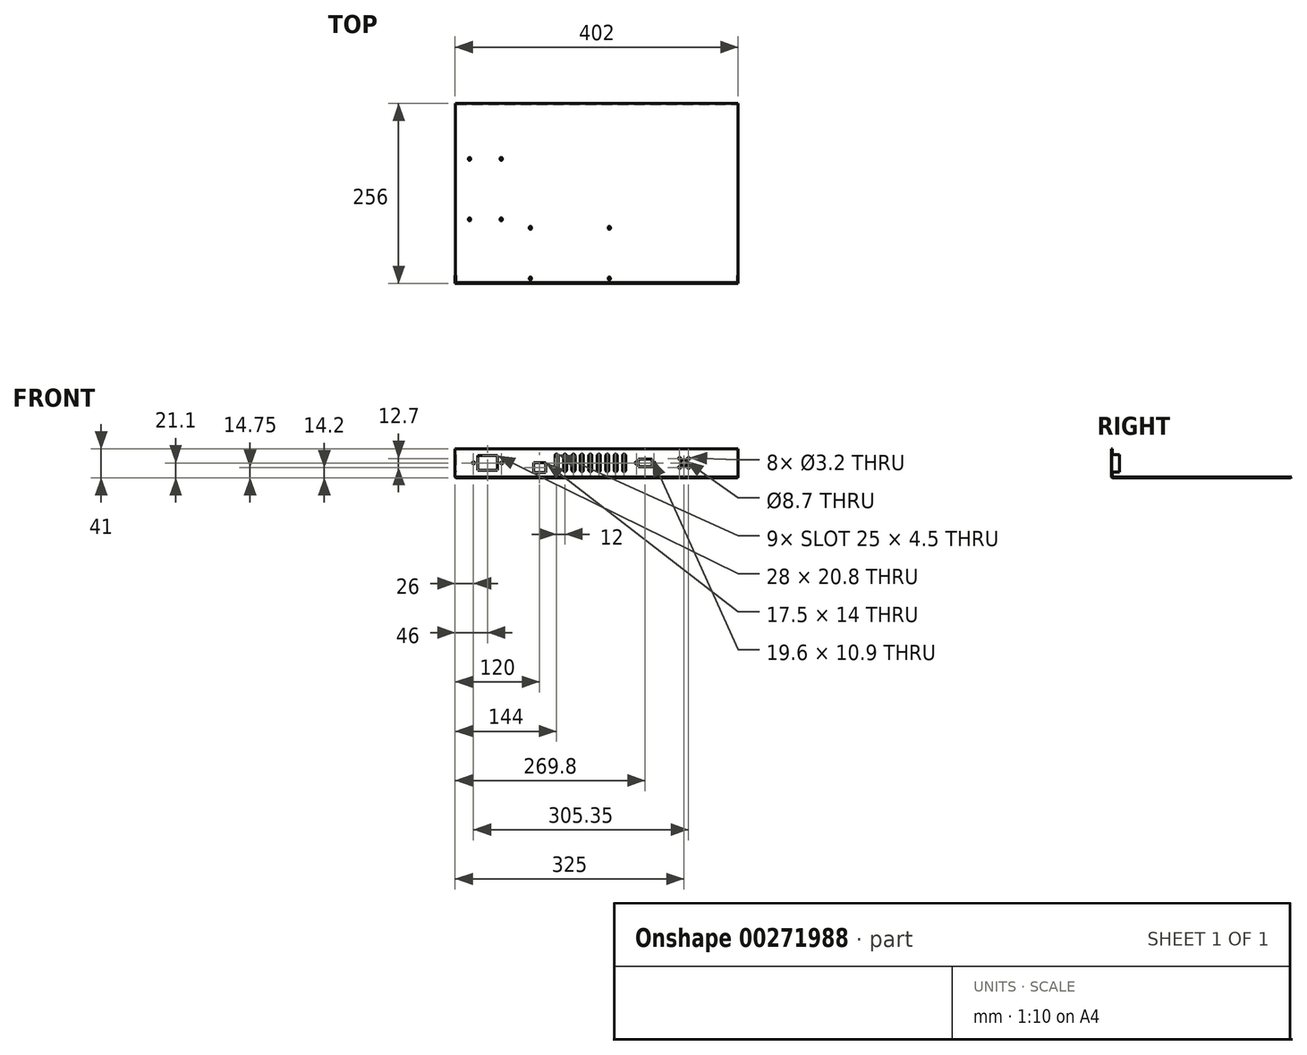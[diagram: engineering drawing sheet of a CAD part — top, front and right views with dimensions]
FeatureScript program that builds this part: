
annotation { "Feature Type Name" : "Feature", "Feature Type Description" : "" }
export const myFeature = defineFeature(function(context is Context, id is Id, definition is map)
    precondition{}
    {
        {
            var Q0;
            Q0=qCreatedBy(makeId("Front.planeOp"),FACE);
            var sketch = newSketch(context, id + "F0", { "sketchPlane" : qUnion([Q0])});
            skLineSegment(sketch, "E0.bottom", {"start": v(0, 0) * mm, "end": v(402, 0) * mm});
            skLineSegment(sketch, "E0.top", {"start": v(0, -41) * mm, "end": v(402, -41) * mm});
            skLineSegment(sketch, "E0.left", {"start": v(0, 0) * mm, "end": v(0, -41) * mm});
            skLineSegment(sketch, "E0.right", {"start": v(402, 0) * mm, "end": v(402, -41) * mm});
            skLineSegment(sketch, "E1.bottom", {"start": v(32, -9.5) * mm, "end": v(60, -9.5) * mm});
            skLineSegment(sketch, "E1.top", {"start": v(32, -30.3) * mm, "end": v(60, -30.3) * mm});
            skLineSegment(sketch, "E1.left", {"start": v(32, -9.5) * mm, "end": v(32, -30.3) * mm});
            skLineSegment(sketch, "E1.right", {"start": v(60, -9.5) * mm, "end": v(60, -30.3) * mm});
            skPoint(sketch, "E2.positionSnap0", {"position": v(60, -19.9) * mm});
            skPoint(sketch, "E3.positionSnap0", {"position": v(32, -19.9) * mm});
            skCircle(sketch, "E4", {"center": v(26, -19.9) * mm, "radius": 1.6 * mm});
            skCircle(sketch, "E5", {"center": v(66, -19.9) * mm, "radius": 1.6 * mm});
            skLineSegment(sketch, "E6.bottom", {"start": v(111.25, -19.8) * mm, "end": v(128.75, -19.8) * mm});
            skLineSegment(sketch, "E6.top", {"start": v(111.25, -33.8) * mm, "end": v(128.75, -33.8) * mm});
            skLineSegment(sketch, "E6.left", {"start": v(111.25, -19.8) * mm, "end": v(111.25, -33.8) * mm});
            skLineSegment(sketch, "E6.right", {"start": v(128.75, -19.8) * mm, "end": v(128.75, -33.8) * mm});
            skCircle(sketch, "E7", {"center": v(325, -19.9) * mm, "radius": 4.35 * mm});
            skLineSegment(sketch, "E8.bottom", {"start": v(260, -14.45) * mm, "end": v(279.6, -14.45) * mm});
            skLineSegment(sketch, "E8.top", {"start": v(260, -25.35) * mm, "end": v(279.6, -25.35) * mm});
            skLineSegment(sketch, "E8.left", {"start": v(260, -14.45) * mm, "end": v(260, -25.35) * mm});
            skLineSegment(sketch, "E8.right", {"start": v(279.6, -14.45) * mm, "end": v(279.6, -25.35) * mm});
            skCircle(sketch, "E9", {"center": v(257.3, -19.9) * mm, "radius": 1.6 * mm});
            skPoint(sketch, "E9.centerSnap0", {"position": v(260, -19.9) * mm});
            skCircle(sketch, "E10", {"center": v(282.3, -19.9) * mm, "radius": 1.6 * mm});
            skPoint(sketch, "E10.centerSnap0", {"position": v(279.6, -19.9) * mm});
            skCircle(sketch, "E11", {"center": v(318.65, -13.55) * mm, "radius": 1.6 * mm});
            skCircle(sketch, "E12", {"center": v(331.35, -13.55) * mm, "radius": 1.6 * mm});
            skCircle(sketch, "E13", {"center": v(331.35, -26.25) * mm, "radius": 1.6 * mm});
            skCircle(sketch, "E14", {"center": v(318.65, -26.25) * mm, "radius": 1.6 * mm});
            skCircle(sketch, "E15", {"center": v(144, -9.65) * mm, "radius": 2.25 * mm});
            skCircle(sketch, "E16", {"center": v(144, -30.15) * mm, "radius": 2.25 * mm});
            skLineSegment(sketch, "E17", {"start": v(146.25, -9.65) * mm, "end": v(146.25, -30.15) * mm});
            skLineSegment(sketch, "E18", {"start": v(146.25, -30.15) * mm, "end": v(141.75, -30.15) * mm});
            skLineSegment(sketch, "E19", {"start": v(141.75, -30.15) * mm, "end": v(141.75, -9.65) * mm});
            skCircle(sketch, "E20", {"center": v(156, -9.65) * mm, "radius": 2.25 * mm});
            skCircle(sketch, "E21", {"center": v(156, -30.15) * mm, "radius": 2.25 * mm});
            skLineSegment(sketch, "E22", {"start": v(158.25, -9.65) * mm, "end": v(158.25, -30.15) * mm});
            skLineSegment(sketch, "E23", {"start": v(153.75, -30.15) * mm, "end": v(153.75, -9.65) * mm});
            skCircle(sketch, "E24", {"center": v(168, -9.65) * mm, "radius": 2.25 * mm});
            skCircle(sketch, "E25", {"center": v(168, -30.15) * mm, "radius": 2.25 * mm});
            skLineSegment(sketch, "E26", {"start": v(170.25, -9.65) * mm, "end": v(170.25, -30.15) * mm});
            skLineSegment(sketch, "E27", {"start": v(165.75, -30.15) * mm, "end": v(165.75, -9.65) * mm});
            skCircle(sketch, "E28", {"center": v(180, -9.65) * mm, "radius": 2.25 * mm});
            skCircle(sketch, "E29", {"center": v(180, -30.15) * mm, "radius": 2.25 * mm});
            skLineSegment(sketch, "E30", {"start": v(182.25, -9.65) * mm, "end": v(182.25, -30.15) * mm});
            skLineSegment(sketch, "E31", {"start": v(177.75, -30.15) * mm, "end": v(177.75, -9.65) * mm});
            skCircle(sketch, "E32", {"center": v(192, -9.65) * mm, "radius": 2.25 * mm});
            skCircle(sketch, "E33", {"center": v(192, -30.15) * mm, "radius": 2.25 * mm});
            skLineSegment(sketch, "E34", {"start": v(194.25, -9.65) * mm, "end": v(194.25, -30.15) * mm});
            skLineSegment(sketch, "E35", {"start": v(189.75, -30.15) * mm, "end": v(189.75, -9.65) * mm});
            skCircle(sketch, "E36", {"center": v(204, -9.65) * mm, "radius": 2.25 * mm});
            skCircle(sketch, "E37", {"center": v(204, -30.15) * mm, "radius": 2.25 * mm});
            skLineSegment(sketch, "E38", {"start": v(206.25, -9.65) * mm, "end": v(206.25, -30.15) * mm});
            skLineSegment(sketch, "E39", {"start": v(201.75, -30.15) * mm, "end": v(201.75, -9.65) * mm});
            skCircle(sketch, "E40", {"center": v(216, -9.65) * mm, "radius": 2.25 * mm});
            skCircle(sketch, "E41", {"center": v(216, -30.15) * mm, "radius": 2.25 * mm});
            skLineSegment(sketch, "E42", {"start": v(218.25, -9.65) * mm, "end": v(218.25, -30.15) * mm});
            skLineSegment(sketch, "E43", {"start": v(213.75, -30.15) * mm, "end": v(213.75, -9.65) * mm});
            skCircle(sketch, "E44", {"center": v(228, -9.65) * mm, "radius": 2.25 * mm});
            skCircle(sketch, "E45", {"center": v(228, -30.15) * mm, "radius": 2.25 * mm});
            skLineSegment(sketch, "E46", {"start": v(230.25, -9.65) * mm, "end": v(230.25, -30.15) * mm});
            skLineSegment(sketch, "E47", {"start": v(225.75, -30.15) * mm, "end": v(225.75, -9.65) * mm});
            skCircle(sketch, "E48", {"center": v(240, -9.65) * mm, "radius": 2.25 * mm});
            skCircle(sketch, "E49", {"center": v(240, -30.15) * mm, "radius": 2.25 * mm});
            skLineSegment(sketch, "E50", {"start": v(242.25, -9.65) * mm, "end": v(242.25, -30.15) * mm});
            skLineSegment(sketch, "E51", {"start": v(237.75, -30.15) * mm, "end": v(237.75, -9.65) * mm});
            skSolve(sketch);
        }
        {
            var Q0;
            Q0=makeQuery(id+"F0.imprint","IMPRINT",FACE,{"disambiguationData":[TD([[makeQuery(id+"F0.imprint","IMPRINT",EDGE,{"derivedFrom":sQuery(id+"F0.wireOp",EDGE,"E0.bottom")}),-1.0]])]});
            extrude(context, id + "F1", {"entities" : qUnion([Q0]), "depth" : 1.1 * mm});
        }
        {
            var Q0;
            Q0=makeQuery(id+"F1.opExtrude","CAP_FACE",FACE,{"disambiguationData":[OSD([sQuery(id+"F0.wireOp",EDGE,"E0.bottom"),sQuery(id+"F0.wireOp",EDGE,"E0.top"),sQuery(id+"F0.wireOp",EDGE,"E0.left"),sQuery(id+"F0.wireOp",EDGE,"E0.right"),sQuery(id+"F0.wireOp",EDGE,"E1.bottom"),sQuery(id+"F0.wireOp",EDGE,"E1.top"),sQuery(id+"F0.wireOp",EDGE,"E1.left"),sQuery(id+"F0.wireOp",EDGE,"E1.right"),sQuery(id+"F0.wireOp",EDGE,"E4"),sQuery(id+"F0.wireOp",EDGE,"E5"),sQuery(id+"F0.wireOp",EDGE,"E6.bottom"),sQuery(id+"F0.wireOp",EDGE,"E6.top"),sQuery(id+"F0.wireOp",EDGE,"E6.left"),sQuery(id+"F0.wireOp",EDGE,"E6.right"),sQuery(id+"F0.wireOp",EDGE,"E7"),sQuery(id+"F0.wireOp",EDGE,"E8.bottom"),sQuery(id+"F0.wireOp",EDGE,"E8.top"),sQuery(id+"F0.wireOp",EDGE,"E8.left"),sQuery(id+"F0.wireOp",EDGE,"E8.right"),sQuery(id+"F0.wireOp",EDGE,"E9"),sQuery(id+"F0.wireOp",EDGE,"E10"),sQuery(id+"F0.wireOp",EDGE,"E11"),sQuery(id+"F0.wireOp",EDGE,"E12"),sQuery(id+"F0.wireOp",EDGE,"E13"),sQuery(id+"F0.wireOp",EDGE,"E14")])],"isStart":true});
            var sketch = newSketch(context, id + "F2", { "sketchPlane" : qUnion([Q0])});
            skLineSegment(sketch, "E52.bottom", {"start": v(0, -7.9) * mm, "end": v(-1.1, -7.9) * mm});
            skLineSegment(sketch, "E52.top", {"start": v(0, -33.1) * mm, "end": v(-1.1, -33.1) * mm});
            skLineSegment(sketch, "E52.left", {"start": v(0, -7.9) * mm, "end": v(0, -33.1) * mm});
            skLineSegment(sketch, "E52.right", {"start": v(-1.1, -7.9) * mm, "end": v(-1.1, -33.1) * mm});
            skLineSegment(sketch, "E53.bottom", {"start": v(-402, -7.9) * mm, "end": v(-400.9, -7.9) * mm});
            skLineSegment(sketch, "E53.top", {"start": v(-402, -33.1) * mm, "end": v(-400.9, -33.1) * mm});
            skLineSegment(sketch, "E53.left", {"start": v(-402, -7.9) * mm, "end": v(-402, -33.1) * mm});
            skLineSegment(sketch, "E53.right", {"start": v(-400.9, -7.9) * mm, "end": v(-400.9, -33.1) * mm});
            skLineSegment(sketch, "E54.bottom", {"start": v(-402, -7.9) * mm, "end": v(-402, -7.9) * mm});
            skLineSegment(sketch, "E54.top", {"start": v(-402, 0) * mm, "end": v(-402, 0) * mm});
            skLineSegment(sketch, "E54.left", {"start": v(-402, -7.9) * mm, "end": v(-402, 0) * mm});
            skLineSegment(sketch, "E54.right", {"start": v(-402, -7.9) * mm, "end": v(-402, 0) * mm});
            skSolve(sketch);
        }
        {
            var Q0;
            Q0=makeQuery(id+"F2.imprint","IMPRINT",FACE,{"disambiguationData":[TD([[makeQuery(id+"F2.imprint","IMPRINT",EDGE,{"derivedFrom":sQuery(id+"F2.wireOp",EDGE,"E53.bottom")}),-1.0]])]});
            var Q1;
            Q1=makeQuery(id+"F2.imprint","IMPRINT",FACE,{"disambiguationData":[TD([[makeQuery(id+"F2.imprint","IMPRINT",EDGE,{"derivedFrom":sQuery(id+"F2.wireOp",EDGE,"E52.bottom")}),1.0]])]});
            extrude(context, id + "F3", {"entities" : qUnion([Q0, Q1]), "operationType" : NewBodyOperationType.ADD, "depth" : 10.1 * mm});
        }
        {
            var Q0;
            Q0=makeQuery(id+"F1.opExtrude","CAP_FACE",FACE,{"disambiguationData":[OSD([sQuery(id+"F0.wireOp",EDGE,"E0.bottom"),sQuery(id+"F0.wireOp",EDGE,"E0.top"),sQuery(id+"F0.wireOp",EDGE,"E0.left"),sQuery(id+"F0.wireOp",EDGE,"E0.right"),sQuery(id+"F0.wireOp",EDGE,"E1.bottom"),sQuery(id+"F0.wireOp",EDGE,"E1.top"),sQuery(id+"F0.wireOp",EDGE,"E1.left"),sQuery(id+"F0.wireOp",EDGE,"E1.right"),sQuery(id+"F0.wireOp",EDGE,"E4"),sQuery(id+"F0.wireOp",EDGE,"E5"),sQuery(id+"F0.wireOp",EDGE,"E6.bottom"),sQuery(id+"F0.wireOp",EDGE,"E6.top"),sQuery(id+"F0.wireOp",EDGE,"E6.left"),sQuery(id+"F0.wireOp",EDGE,"E6.right"),sQuery(id+"F0.wireOp",EDGE,"E7"),sQuery(id+"F0.wireOp",EDGE,"E8.bottom"),sQuery(id+"F0.wireOp",EDGE,"E8.top"),sQuery(id+"F0.wireOp",EDGE,"E8.left"),sQuery(id+"F0.wireOp",EDGE,"E8.right"),sQuery(id+"F0.wireOp",EDGE,"E9"),sQuery(id+"F0.wireOp",EDGE,"E10"),sQuery(id+"F0.wireOp",EDGE,"E11"),sQuery(id+"F0.wireOp",EDGE,"E12"),sQuery(id+"F0.wireOp",EDGE,"E13"),sQuery(id+"F0.wireOp",EDGE,"E14")])],"isStart":true});
            var sketch = newSketch(context, id + "F4", { "sketchPlane" : qUnion([Q0])});
            skLineSegment(sketch, "E55.bottom", {"start": v(0, -41) * mm, "end": v(-402, -41) * mm});
            skLineSegment(sketch, "E55.top", {"start": v(0, -39.9) * mm, "end": v(-402, -39.9) * mm});
            skLineSegment(sketch, "E55.left", {"start": v(0, -41) * mm, "end": v(0, -39.9) * mm});
            skLineSegment(sketch, "E55.right", {"start": v(-402, -41) * mm, "end": v(-402, -39.9) * mm});
            skSolve(sketch);
        }
        {
            var Q0;
            Q0=makeQuery(id+"F4.imprint","IMPRINT",FACE,{"disambiguationData":[TD([[makeQuery(id+"F4.imprint","IMPRINT",EDGE,{"derivedFrom":sQuery(id+"F4.wireOp",EDGE,"E55.bottom")}),-1.0]])]});
            extrude(context, id + "F5", {"entities" : qUnion([Q0]), "operationType" : NewBodyOperationType.ADD, "depth" : 255 * mm});
        }
        {
            var Q0;
            Q0=makeQuery(id+"F5.opExtrude","SWEPT_FACE",FACE,{"disambiguationData":[OSD([sQuery(id+"F4.wireOp",EDGE,"E55.top")])]});
            var sketch = newSketch(context, id + "F6", { "sketchPlane" : qUnion([Q0])});
            skCircle(sketch, "E56", {"center": v(65.5, 90) * mm, "radius": 1.6 * mm});
            skCircle(sketch, "E57", {"center": v(20.5, 90) * mm, "radius": 1.6 * mm});
            skCircle(sketch, "E58", {"center": v(20.5, 176) * mm, "radius": 1.6 * mm});
            skCircle(sketch, "E59", {"center": v(65.5, 176) * mm, "radius": 1.6 * mm});
            skSolve(sketch);
        }
        {
            var Q0;
            Q0=sQuery(id+"F6.wireOp",VERTEX,"E57.center");
            var Q1;
            Q1=sQuery(id+"F6.wireOp",VERTEX,"E56.center");
            var Q2;
            Q2=sQuery(id+"F6.wireOp",VERTEX,"E59.center");
            var Q3;
            Q3=sQuery(id+"F6.wireOp",VERTEX,"E58.center");
            var Q4;
            Q4=makeQuery(id+"F1.opExtrude","SWEPT_BODY",BODY,{"disambiguationData":[OSD([sQuery(id+"F0.wireOp",EDGE,"E0.bottom"),sQuery(id+"F0.wireOp",EDGE,"E0.top"),sQuery(id+"F0.wireOp",EDGE,"E0.left"),sQuery(id+"F0.wireOp",EDGE,"E0.right"),sQuery(id+"F0.wireOp",EDGE,"E1.bottom"),sQuery(id+"F0.wireOp",EDGE,"E1.top"),sQuery(id+"F0.wireOp",EDGE,"E1.left"),sQuery(id+"F0.wireOp",EDGE,"E1.right"),sQuery(id+"F0.wireOp",EDGE,"E4"),sQuery(id+"F0.wireOp",EDGE,"E5"),sQuery(id+"F0.wireOp",EDGE,"E6.bottom"),sQuery(id+"F0.wireOp",EDGE,"E6.top"),sQuery(id+"F0.wireOp",EDGE,"E6.left"),sQuery(id+"F0.wireOp",EDGE,"E6.right"),sQuery(id+"F0.wireOp",EDGE,"E7"),sQuery(id+"F0.wireOp",EDGE,"E8.bottom"),sQuery(id+"F0.wireOp",EDGE,"E8.top"),sQuery(id+"F0.wireOp",EDGE,"E8.left"),sQuery(id+"F0.wireOp",EDGE,"E8.right"),sQuery(id+"F0.wireOp",EDGE,"E9"),sQuery(id+"F0.wireOp",EDGE,"E10"),sQuery(id+"F0.wireOp",EDGE,"E11"),sQuery(id+"F0.wireOp",EDGE,"E12"),sQuery(id+"F0.wireOp",EDGE,"E13"),sQuery(id+"F0.wireOp",EDGE,"E14"),sQuery(id+"F0.wireOp",EDGE,"E15"),sQuery(id+"F0.wireOp",EDGE,"E16"),sQuery(id+"F0.wireOp",EDGE,"E17"),sQuery(id+"F0.wireOp",EDGE,"E19"),sQuery(id+"F0.wireOp",EDGE,"E20"),sQuery(id+"F0.wireOp",EDGE,"E21"),sQuery(id+"F0.wireOp",EDGE,"E22"),sQuery(id+"F0.wireOp",EDGE,"E23"),sQuery(id+"F0.wireOp",EDGE,"E24"),sQuery(id+"F0.wireOp",EDGE,"E25"),sQuery(id+"F0.wireOp",EDGE,"E26"),sQuery(id+"F0.wireOp",EDGE,"E27"),sQuery(id+"F0.wireOp",EDGE,"E28"),sQuery(id+"F0.wireOp",EDGE,"E29"),sQuery(id+"F0.wireOp",EDGE,"E30"),sQuery(id+"F0.wireOp",EDGE,"E31"),sQuery(id+"F0.wireOp",EDGE,"E32"),sQuery(id+"F0.wireOp",EDGE,"E33"),sQuery(id+"F0.wireOp",EDGE,"E34"),sQuery(id+"F0.wireOp",EDGE,"E35"),sQuery(id+"F0.wireOp",EDGE,"E36"),sQuery(id+"F0.wireOp",EDGE,"E37"),sQuery(id+"F0.wireOp",EDGE,"E38"),sQuery(id+"F0.wireOp",EDGE,"E39"),sQuery(id+"F0.wireOp",EDGE,"E40"),sQuery(id+"F0.wireOp",EDGE,"E41"),sQuery(id+"F0.wireOp",EDGE,"E42"),sQuery(id+"F0.wireOp",EDGE,"E43"),sQuery(id+"F0.wireOp",EDGE,"E44"),sQuery(id+"F0.wireOp",EDGE,"E45"),sQuery(id+"F0.wireOp",EDGE,"E46"),sQuery(id+"F0.wireOp",EDGE,"E47"),sQuery(id+"F0.wireOp",EDGE,"E48"),sQuery(id+"F0.wireOp",EDGE,"E49"),sQuery(id+"F0.wireOp",EDGE,"E50"),sQuery(id+"F0.wireOp",EDGE,"E51")])]});
            hole(context, id + "F7", {"style" : HoleStyle.SIMPLE, "endStyle" : HoleEndStyle.THROUGH, "holeDiameter" : 3.2 * mm, "tappedDepth" : 12 * mm, "tapClearance" : 3, "locations" : qUnion([Q0, Q1, Q2, Q3]), "scope" : qUnion([Q4])});
        }
        {
            var Q0;
            Q0=makeQuery(id+"F5.opExtrude","SWEPT_FACE",FACE,{"disambiguationData":[OSD([sQuery(id+"F4.wireOp",EDGE,"E55.top")])]});
            var sketch = newSketch(context, id + "F8", { "sketchPlane" : qUnion([Q0])});
            skLineSegment(sketch, "E60.bottom", {"start": v(106.95, 6) * mm, "end": v(218.95, 6) * mm});
            skLineSegment(sketch, "E60.top", {"start": v(106.95, 78) * mm, "end": v(218.95, 78) * mm});
            skLineSegment(sketch, "E60.left", {"start": v(106.95, 6) * mm, "end": v(106.95, 78) * mm});
            skLineSegment(sketch, "E60.right", {"start": v(218.95, 6) * mm, "end": v(218.95, 78) * mm});
            skCircle(sketch, "E61", {"center": v(218.95, 6) * mm, "radius": 1.6 * mm});
            skCircle(sketch, "E62", {"center": v(218.95, 78) * mm, "radius": 1.6 * mm});
            skCircle(sketch, "E63", {"center": v(106.95, 78) * mm, "radius": 1.6 * mm});
            skCircle(sketch, "E64", {"center": v(106.95, 6) * mm, "radius": 1.6 * mm});
            skSolve(sketch);
        }
        {
            var Q0;
            Q0=sQuery(id+"F8.wireOp",VERTEX,"E64.center");
            var Q1;
            Q1=sQuery(id+"F8.wireOp",VERTEX,"E63.center");
            var Q2;
            Q2=sQuery(id+"F8.wireOp",VERTEX,"E61.center");
            var Q3;
            Q3=sQuery(id+"F8.wireOp",VERTEX,"E62.center");
            var Q4;
            Q4=makeQuery(id+"F1.opExtrude","SWEPT_BODY",BODY,{"disambiguationData":[OSD([sQuery(id+"F0.wireOp",EDGE,"E0.bottom"),sQuery(id+"F0.wireOp",EDGE,"E0.top"),sQuery(id+"F0.wireOp",EDGE,"E0.left"),sQuery(id+"F0.wireOp",EDGE,"E0.right"),sQuery(id+"F0.wireOp",EDGE,"E1.bottom"),sQuery(id+"F0.wireOp",EDGE,"E1.top"),sQuery(id+"F0.wireOp",EDGE,"E1.left"),sQuery(id+"F0.wireOp",EDGE,"E1.right"),sQuery(id+"F0.wireOp",EDGE,"E4"),sQuery(id+"F0.wireOp",EDGE,"E5"),sQuery(id+"F0.wireOp",EDGE,"E6.bottom"),sQuery(id+"F0.wireOp",EDGE,"E6.top"),sQuery(id+"F0.wireOp",EDGE,"E6.left"),sQuery(id+"F0.wireOp",EDGE,"E6.right"),sQuery(id+"F0.wireOp",EDGE,"E7"),sQuery(id+"F0.wireOp",EDGE,"E8.bottom"),sQuery(id+"F0.wireOp",EDGE,"E8.top"),sQuery(id+"F0.wireOp",EDGE,"E8.left"),sQuery(id+"F0.wireOp",EDGE,"E8.right"),sQuery(id+"F0.wireOp",EDGE,"E9"),sQuery(id+"F0.wireOp",EDGE,"E10"),sQuery(id+"F0.wireOp",EDGE,"E11"),sQuery(id+"F0.wireOp",EDGE,"E12"),sQuery(id+"F0.wireOp",EDGE,"E13"),sQuery(id+"F0.wireOp",EDGE,"E14"),sQuery(id+"F0.wireOp",EDGE,"E15"),sQuery(id+"F0.wireOp",EDGE,"E16"),sQuery(id+"F0.wireOp",EDGE,"E17"),sQuery(id+"F0.wireOp",EDGE,"E19"),sQuery(id+"F0.wireOp",EDGE,"E20"),sQuery(id+"F0.wireOp",EDGE,"E21"),sQuery(id+"F0.wireOp",EDGE,"E22"),sQuery(id+"F0.wireOp",EDGE,"E23"),sQuery(id+"F0.wireOp",EDGE,"E24"),sQuery(id+"F0.wireOp",EDGE,"E25"),sQuery(id+"F0.wireOp",EDGE,"E26"),sQuery(id+"F0.wireOp",EDGE,"E27"),sQuery(id+"F0.wireOp",EDGE,"E28"),sQuery(id+"F0.wireOp",EDGE,"E29"),sQuery(id+"F0.wireOp",EDGE,"E30"),sQuery(id+"F0.wireOp",EDGE,"E31"),sQuery(id+"F0.wireOp",EDGE,"E32"),sQuery(id+"F0.wireOp",EDGE,"E33"),sQuery(id+"F0.wireOp",EDGE,"E34"),sQuery(id+"F0.wireOp",EDGE,"E35"),sQuery(id+"F0.wireOp",EDGE,"E36"),sQuery(id+"F0.wireOp",EDGE,"E37"),sQuery(id+"F0.wireOp",EDGE,"E38"),sQuery(id+"F0.wireOp",EDGE,"E39"),sQuery(id+"F0.wireOp",EDGE,"E40"),sQuery(id+"F0.wireOp",EDGE,"E41"),sQuery(id+"F0.wireOp",EDGE,"E42"),sQuery(id+"F0.wireOp",EDGE,"E43"),sQuery(id+"F0.wireOp",EDGE,"E44"),sQuery(id+"F0.wireOp",EDGE,"E45"),sQuery(id+"F0.wireOp",EDGE,"E46"),sQuery(id+"F0.wireOp",EDGE,"E47"),sQuery(id+"F0.wireOp",EDGE,"E48"),sQuery(id+"F0.wireOp",EDGE,"E49"),sQuery(id+"F0.wireOp",EDGE,"E50"),sQuery(id+"F0.wireOp",EDGE,"E51")])]});
            hole(context, id + "F9", {"style" : HoleStyle.SIMPLE, "endStyle" : HoleEndStyle.THROUGH, "holeDiameter" : 3.2 * mm, "tappedDepth" : 12 * mm, "tapClearance" : 3, "locations" : qUnion([Q0, Q1, Q2, Q3]), "scope" : qUnion([Q4])});
        }
        {
            var Q0;
            Q0=makeQuery(id+"F5.boolean.opBoolean","MERGE",FACE,{"derivedFrom":[makeQuery(id+"F1.opExtrude","SWEPT_FACE",FACE,{"disambiguationData":[OSD([sQuery(id+"F0.wireOp",EDGE,"E0.top")])]}),makeQuery(id+"F5.opExtrude","SWEPT_FACE",FACE,{"disambiguationData":[OSD([sQuery(id+"F4.wireOp",EDGE,"E55.bottom")])]})]});
            chamfer(context, id + "F10", {"entities" : qUnion([Q0]), "width" : 1.2 * mm, "tangentPropagation" : true});
        }
    });
